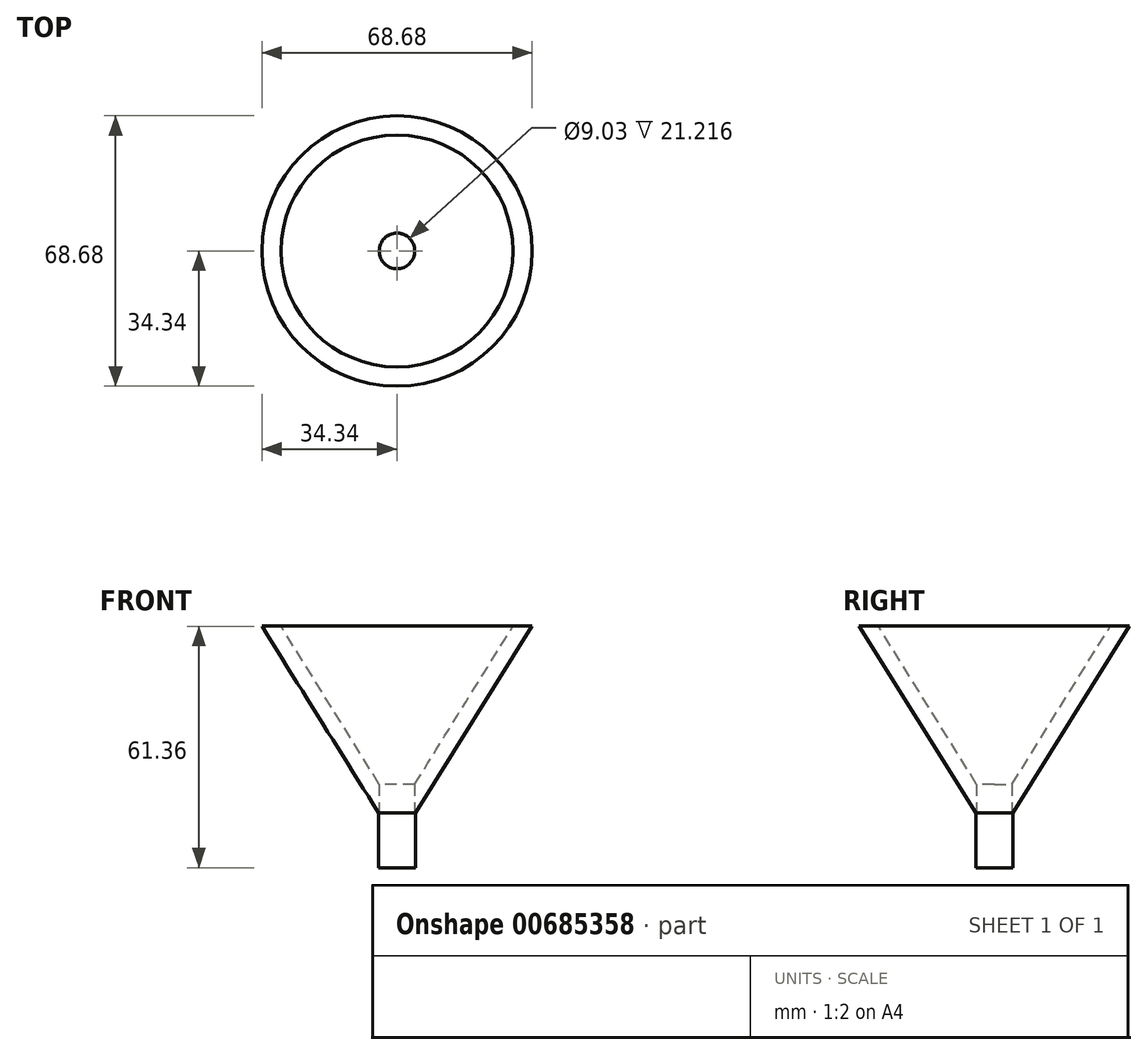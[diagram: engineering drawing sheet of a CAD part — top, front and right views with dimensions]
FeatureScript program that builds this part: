
annotation { "Feature Type Name" : "Feature", "Feature Type Description" : "" }
export const myFeature = defineFeature(function(context is Context, id is Id, definition is map)
    precondition{}
    {
        {
            var Q0;
            Q0=qCreatedBy(makeId("Front.planeOp"),FACE);
            var sketch = newSketch(context, id + "F0", { "sketchPlane" : qUnion([Q0])});
            skLineSegment(sketch, "E0", {"start": v(0, -13.95) * mm, "end": v(0, 0) * mm});
            skLineSegment(sketch, "E1", {"start": v(0, 0) * mm, "end": v(29.46, 47.41) * mm});
            skLineSegment(sketch, "E2", {"start": v(29.46, 47.41) * mm, "end": v(34.34, 47.41) * mm});
            skLineSegment(sketch, "E3", {"start": v(34.34, 47.41) * mm, "end": v(4.7, 0) * mm});
            skLineSegment(sketch, "E4", {"start": v(4.7, 0) * mm, "end": v(4.7, -13.95) * mm});
            skLineSegment(sketch, "E5", {"start": v(4.7, -13.95) * mm, "end": v(0, -13.95) * mm});
            skSolve(sketch);
        }
        {
            var Q0;
            Q0=makeQuery(id+"F0.imprint","IMPRINT",FACE,{"disambiguationData":[TD([[makeQuery(id+"F0.imprint","IMPRINT",EDGE,{"derivedFrom":sQuery(id+"F0.wireOp",EDGE,"E0")}),-1.0]])]});
            var Q1;
            Q1=sQuery(id+"F0.wireOp",EDGE,"E0");
            revolve(context, id + "F1", {"surfaceOperationType" : NewSurfaceOperationType.NEW, "entities" : qUnion([Q0]), "axis" : qUnion([Q1]), "revolveType" : RevolveType.FULL});
        }
        {
            var Q0;
            Q0=makeQuery(id+"F1.opRevolve","SWEPT_FACE",FACE,{"disambiguationData":[OSD([sQuery(id+"F0.wireOp",EDGE,"E5")])]});
            var sketch = newSketch(context, id + "F2", { "sketchPlane" : qUnion([Q0])});
            skCircle(sketch, "E6", {"center": v(0, 0) * mm, "radius": 4.52 * mm});
            skSolve(sketch);
        }
        {
            var Q0;
            Q0 = qSketchRegion(id + "F2", true);
            extrude(context, id + "F3", {"entities" : qUnion([Q0]), "operationType" : NewBodyOperationType.REMOVE, "oppositeDirection" : true, "depth" : 25.4 * mm, "offsetDistance" : 25.4 * mm});
        }
    });
